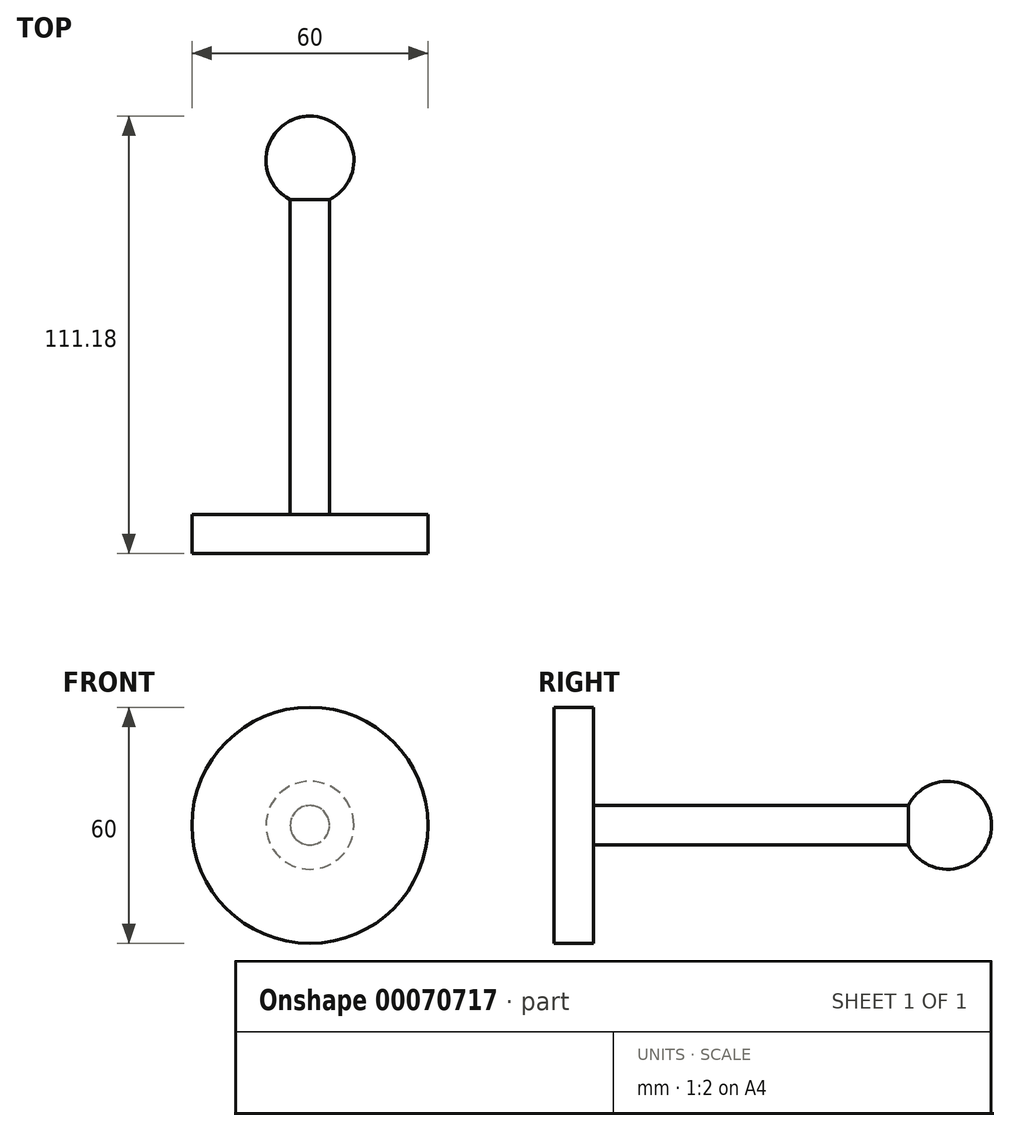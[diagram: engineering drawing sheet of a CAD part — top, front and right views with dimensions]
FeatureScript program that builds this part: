
annotation { "Feature Type Name" : "Feature", "Feature Type Description" : "" }
export const myFeature = defineFeature(function(context is Context, id is Id, definition is map)
    precondition{}
    {
        {
            var Q0;
            Q0=qCreatedBy(makeId("Top.planeOp"),FACE);
            var sketch = newSketch(context, id + "F0", { "sketchPlane" : qUnion([Q0])});
            skLineSegment(sketch, "E0", {"start": v(0, 0) * mm, "end": v(0, 100) * mm});
            skLineSegment(sketch, "E1", {"start": v(0, 0) * mm, "end": v(-30, 0) * mm});
            skLineSegment(sketch, "E2", {"start": v(-30, 0) * mm, "end": v(-30, 10) * mm});
            skLineSegment(sketch, "E3", {"start": v(-30, 10) * mm, "end": v(-5, 10) * mm});
            skLineSegment(sketch, "E4", {"start": v(-5, 10) * mm, "end": v(-5, 90) * mm});
            skArc(sketch, "E5", {"start": v(-5, 90) * mm, "mid": v(-10.88, 102.57) * mm, "end": v(0, 111.18) * mm});
            skLineSegment(sketch, "E6", {"start": v(0, 100) * mm, "end": v(0, 111.18) * mm});
            skSolve(sketch);
        }
        {
            var Q0;
            Q0 = qSketchRegion(id + "F0", true);
            var Q1;
            Q1=sQuery(id+"F0.wireOp",EDGE,"E0");
            revolve(context, id + "F1", {"entities" : qUnion([Q0]), "axis" : qUnion([Q1]), "revolveType" : RevolveType.FULL});
        }
    });
